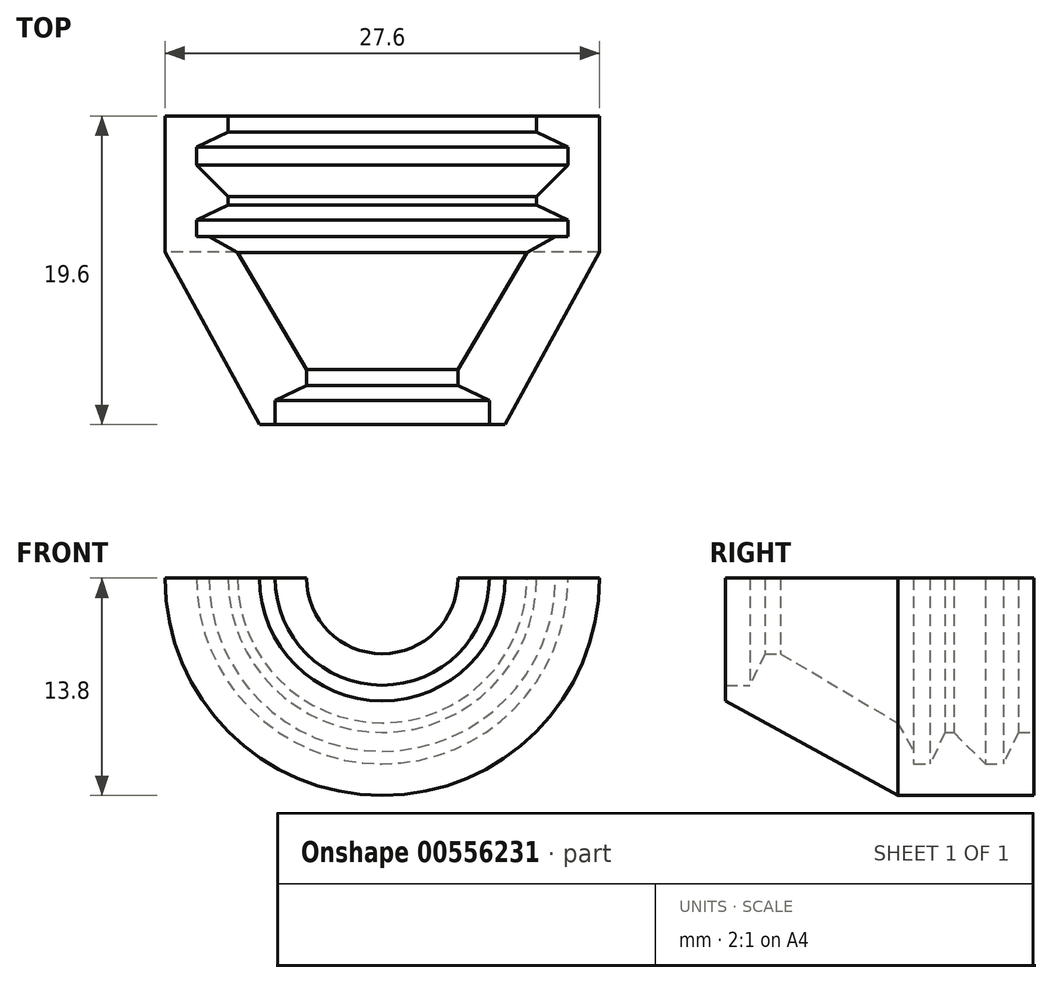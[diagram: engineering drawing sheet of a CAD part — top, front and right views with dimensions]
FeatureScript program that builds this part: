
annotation { "Feature Type Name" : "Feature", "Feature Type Description" : "" }
export const myFeature = defineFeature(function(context is Context, id is Id, definition is map)
    precondition{}
    {
        {
            var Q0;
            Q0=qCreatedBy(makeId("Top.planeOp"),FACE);
            var sketch = newSketch(context, id + "F0", { "sketchPlane" : qUnion([Q0])});
            skLineSegment(sketch, "E0", {"start": v(-11.8, 6.65) * mm, "end": v(-11.8, 5.65) * mm});
            skLineSegment(sketch, "E1", {"start": v(-11.8, 5.65) * mm, "end": v(-9.8, 5.65) * mm});
            skLineSegment(sketch, "E2", {"start": v(-9.8, 2) * mm, "end": v(-11.8, 2) * mm});
            skLineSegment(sketch, "E3", {"start": v(-11.8, 2) * mm, "end": v(-11.8, 1) * mm});
            skLineSegment(sketch, "E4", {"start": v(-11.8, 1) * mm, "end": v(-9.8, 1) * mm});
            skLineSegment(sketch, "E5", {"start": v(-4.8, -9.45) * mm, "end": v(-6.8, -9.45) * mm});
            skLineSegment(sketch, "E6", {"start": v(-6.8, -9.45) * mm, "end": v(-6.8, -10.95) * mm});
            skLineSegment(sketch, "E7", {"start": v(0, 15) * mm, "end": v(0, -15) * mm});
            skLineSegment(sketch, "E8", {"start": v(-9.8, 2) * mm, "end": v(-9.8, 5.65) * mm});
            skLineSegment(sketch, "E9", {"start": v(-13.8, 6.65) * mm, "end": v(-13.8, 0) * mm});
            skLineSegment(sketch, "E10", {"start": v(-13.8, 0) * mm, "end": v(-7.8, -10.95) * mm});
            skLineSegment(sketch, "E11", {"start": v(-4.8, -9.45) * mm, "end": v(-4.8, -7.45) * mm});
            skLineSegment(sketch, "E12", {"start": v(-7.8, -10.95) * mm, "end": v(-6.8, -10.95) * mm});
            skLineSegment(sketch, "E13", {"start": v(-11.8, 6.65) * mm, "end": v(-13.8, 6.65) * mm});
            skLineSegment(sketch, "E14", {"start": v(-9.8, 1) * mm, "end": v(-4.8, -7.45) * mm});
            skLineSegment(sketch, "E15.bottom", {"start": v(-13.8, 6.65) * mm, "end": v(-9.8, 6.65) * mm});
            skLineSegment(sketch, "E15.top", {"start": v(-13.8, 8.65) * mm, "end": v(-9.8, 8.65) * mm});
            skLineSegment(sketch, "E15.left", {"start": v(-13.8, 6.65) * mm, "end": v(-13.8, 8.65) * mm});
            skLineSegment(sketch, "E15.right", {"start": v(-9.8, 6.65) * mm, "end": v(-9.8, 8.65) * mm});
            skSolve(sketch);
        }
        {
            var Q0;
            Q0=makeQuery(id+"F0.imprint","IMPRINT",FACE,{"disambiguationData":[TD([[makeQuery(id+"F0.imprint","IMPRINT",EDGE,{"derivedFrom":sQuery(id+"F0.wireOp",EDGE,"E0")}),-1.0]])]});
            var Q1;
            Q1=makeQuery(id+"F0.imprint","IMPRINT",FACE,{"disambiguationData":[TD([[makeQuery(id+"F0.imprint","IMPRINT",EDGE,{"derivedFrom":sQuery(id+"F0.wireOp",EDGE,"E15.top")}),-1.0]])]});
            var Q2;
            Q2=sQuery(id+"F0.wireOp",EDGE,"E7");
            revolve(context, id + "F1", {"entities" : qUnion([Q0, Q1]), "axis" : qUnion([Q2]), "revolveType" : RevolveType.ONE_DIRECTION, "angle" : 180 * degree});
        }
        {
            var Q0;
            Q0=makeQuery(id+"F1.opRevolve","SWEPT_EDGE",EDGE,{"disambiguationData":[OSD([sQuery(id+"F0.wireOp",EDGE,"E4"),sQuery(id+"F0.wireOp",EDGE,"E14")])]});
            chamfer(context, id + "F2", {"entities" : qUnion([Q0]), "width" : 2.1 * mm, "tangentPropagation" : true});
        }
        {
            var Q0;
            Q0=makeQuery(id+"F1.opRevolve","SWEPT_EDGE",EDGE,{"disambiguationData":[OSD([sQuery(id+"F0.wireOp",EDGE,"E1"),sQuery(id+"F0.wireOp",EDGE,"E8")])]});
            chamfer(context, id + "F3", {"entities" : qUnion([Q0]), "width" : 2.1 * mm, "tangentPropagation" : true});
        }
        {
            var Q0;
            Q0=makeQuery(id+"F1.opRevolve","SWEPT_EDGE",EDGE,{"disambiguationData":[OSD([sQuery(id+"F0.wireOp",EDGE,"E15.bottom"),sQuery(id+"F0.wireOp",EDGE,"E15.right")])]});
            chamfer(context, id + "F4", {"entities" : qUnion([Q0]), "chamferType" : ChamferType.TWO_OFFSETS, "width1" : 2.1 * mm, "oppositeDirection" : false, "width2" : 1 * mm, "tangentPropagation" : true});
        }
        {
            var Q0;
            Q0=makeQuery(id+"F1.opRevolve","SWEPT_EDGE",EDGE,{"disambiguationData":[OSD([sQuery(id+"F0.wireOp",EDGE,"E2"),sQuery(id+"F0.wireOp",EDGE,"E8")])]});
            chamfer(context, id + "F5", {"entities" : qUnion([Q0]), "chamferType" : ChamferType.TWO_OFFSETS, "width1" : 2.1 * mm, "oppositeDirection" : false, "width2" : 1 * mm, "tangentPropagation" : true});
        }
        {
            var Q0;
            Q0=makeQuery(id+"F1.opRevolve","SWEPT_EDGE",EDGE,{"disambiguationData":[OSD([sQuery(id+"F0.wireOp",EDGE,"E5"),sQuery(id+"F0.wireOp",EDGE,"E11")])]});
            chamfer(context, id + "F6", {"entities" : qUnion([Q0]), "chamferType" : ChamferType.TWO_OFFSETS, "width1" : 2.1 * mm, "oppositeDirection" : false, "width2" : 1 * mm, "tangentPropagation" : true});
        }
    });
